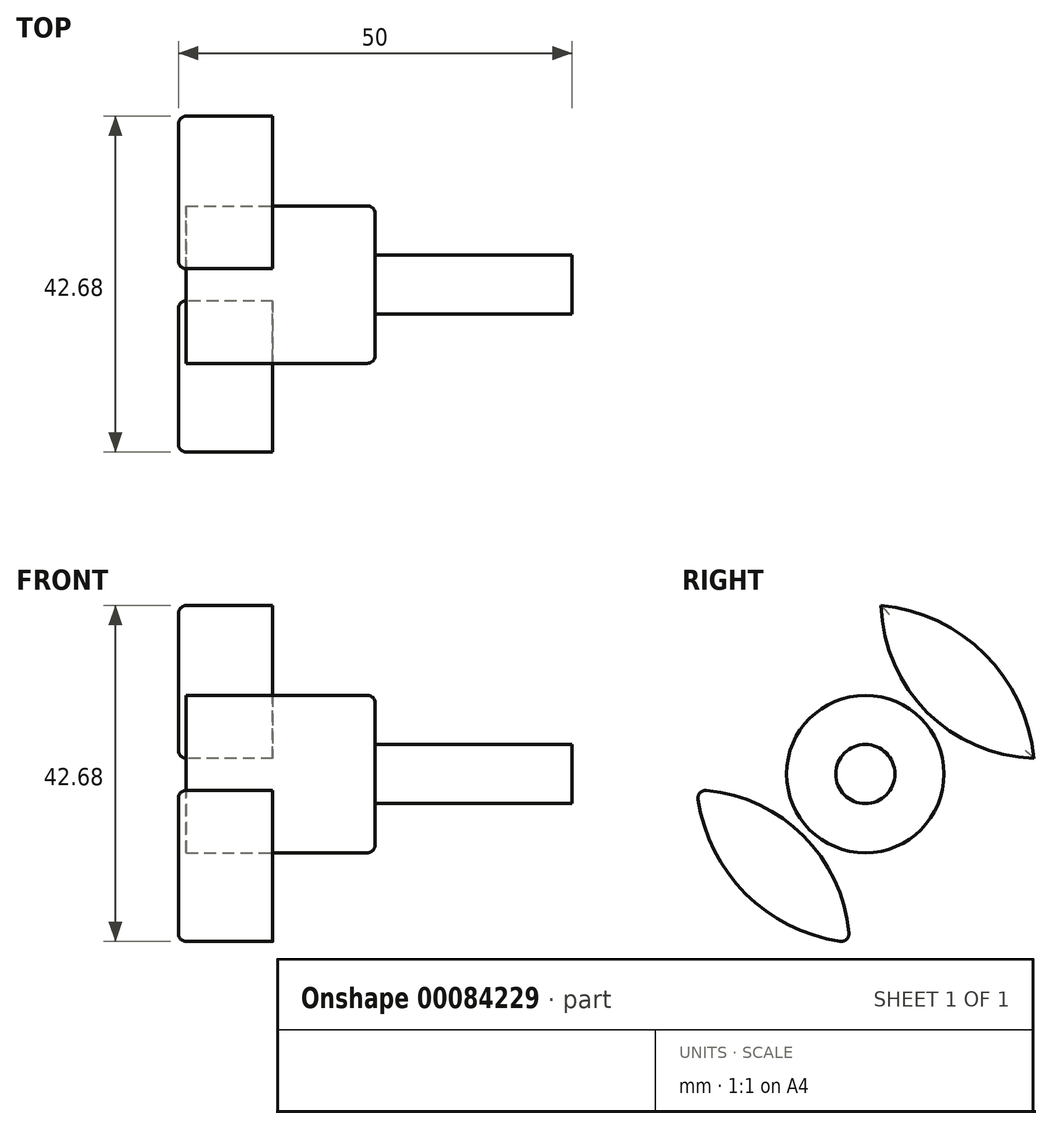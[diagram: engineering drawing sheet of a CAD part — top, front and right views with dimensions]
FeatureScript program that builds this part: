
annotation { "Feature Type Name" : "Feature", "Feature Type Description" : "" }
export const myFeature = defineFeature(function(context is Context, id is Id, definition is map)
    precondition{}
    {
        {
            var Q0;
            Q0=qCreatedBy(makeId("Front.planeOp"),FACE);
            var sketch = newSketch(context, id + "F0", { "sketchPlane" : qUnion([Q0])});
            skLineSegment(sketch, "E0.bottom", {"start": v(0, 0) * mm, "end": v(-25, 0) * mm});
            skLineSegment(sketch, "E0.top", {"start": v(0, 3.75) * mm, "end": v(-25, 3.75) * mm});
            skLineSegment(sketch, "E0.left", {"start": v(0, 0) * mm, "end": v(0, 3.75) * mm});
            skLineSegment(sketch, "E0.right", {"start": v(-25, 0) * mm, "end": v(-25, 3.75) * mm});
            skLineSegment(sketch, "E1.bottom", {"start": v(-25, 0) * mm, "end": v(-38, 0) * mm});
            skLineSegment(sketch, "E1.top", {"start": v(-25, 10) * mm, "end": v(-38, 10) * mm});
            skLineSegment(sketch, "E1.left", {"start": v(-25, 0) * mm, "end": v(-25, 10) * mm});
            skLineSegment(sketch, "E1.right", {"start": v(-38, 0) * mm, "end": v(-38, 10) * mm});
            skLineSegment(sketch, "E2.bottom", {"start": v(-38, 0) * mm, "end": v(-50, 0) * mm});
            skLineSegment(sketch, "E2.top", {"start": v(-38, 21.5) * mm, "end": v(-50, 21.5) * mm});
            skLineSegment(sketch, "E2.left", {"start": v(-38, 0) * mm, "end": v(-38, 21.5) * mm});
            skLineSegment(sketch, "E2.right", {"start": v(-50, 0) * mm, "end": v(-50, 21.5) * mm});
            skLineSegment(sketch, "E3", {"start": v(0, 0) * mm, "end": v(-63.49, 0) * mm, "construction": true});
            skSolve(sketch);
        }
        {
            var Q0;
            {var subQ3=sQuery(id+"F0.wireOp",EDGE,"E2.bottom");Q0=makeQuery(id+"F0.imprint","IMPRINT",FACE,{"disambiguationData":[TD([[makeQuery(id+"F0.imprint","IMPRINT",EDGE,{"derivedFrom":subQ3}),-1.0]])]});}
            var Q1;
            {var subQ3=sQuery(id+"F0.wireOp",EDGE,"E1.bottom");Q1=makeQuery(id+"F0.imprint","IMPRINT",FACE,{"disambiguationData":[TD([[makeQuery(id+"F0.imprint","IMPRINT",EDGE,{"derivedFrom":subQ3}),-1.0]])]});}
            var Q2;
            {var subQ0=sQuery(id+"F0.wireOp",EDGE,"E0.bottom");Q2=makeQuery(id+"F0.imprint","IMPRINT",FACE,{"disambiguationData":[TD([[makeQuery(id+"F0.imprint","IMPRINT",EDGE,{"derivedFrom":subQ0}),-1.0]])]});}
            var Q3;
            Q3=sQuery(id+"F0.wireOp",EDGE,"E3");
            revolve(context, id + "F1", {"entities" : qUnion([Q0, Q1, Q2]), "axis" : qUnion([Q3]), "revolveType" : RevolveType.FULL});
        }
        {
            var Q0;
            Q0=makeQuery(id+"F1.opRevolve","SWEPT_FACE",FACE,{"disambiguationData":[OSD([sQuery(id+"F0.wireOp",EDGE,"E2.right")])]});
            var sketch = newSketch(context, id + "F2", { "sketchPlane" : qUnion([Q0])});
            skCircle(sketch, "E4.0", {"center": v(0, 0) * mm, "radius": 10 * mm});
            skCircle(sketch, "E5.0", {"center": v(0, 0) * mm, "radius": 21.5 * mm});
            skLineSegment(sketch, "E6", {"start": v(0, 21.5) * mm, "end": v(0, -21.5) * mm, "construction": true});
            skLineSegment(sketch, "E7", {"start": v(21.5, 0) * mm, "end": v(-21.5, 0) * mm, "construction": true});
            skLineSegment(sketch, "E8", {"start": v(0, 0) * mm, "end": v(15.2, 15.2) * mm, "construction": true});
            skArc(sketch, "E9", {"start": v(2, 21.4) * mm, "mid": v(7.85, 7.85) * mm, "end": v(21.4, 2) * mm});
            skArc(sketch, "E10.MirrorCS", {"start": v(2, -21.4) * mm, "mid": v(7.85, -7.85) * mm, "end": v(21.4, -2) * mm});
            skArc(sketch, "E11.MirrorCS", {"start": v(-2, 21.4) * mm, "mid": v(-7.85, 7.85) * mm, "end": v(-21.4, 2) * mm});
            skArc(sketch, "E12.MirrorCS", {"start": v(-2, -21.4) * mm, "mid": v(-7.85, -7.85) * mm, "end": v(-21.4, -2) * mm});
            skSolve(sketch);
        }
        {
            var Q0;
            {var subQ0=sQuery(id+"F2.wireOp",EDGE,"E11.MirrorCS");Q0=makeQuery(id+"F2.imprint","IMPRINT",FACE,{"disambiguationData":[TD([[makeQuery(id+"F2.imprint","IMPRINT",EDGE,{"derivedFrom":subQ0}),-1.0]])]});}
            var Q1;
            {var subQ0=sQuery(id+"F2.wireOp",EDGE,"E9");Q1=makeQuery(id+"F2.imprint","IMPRINT",FACE,{"disambiguationData":[TD([[makeQuery(id+"F2.imprint","IMPRINT",EDGE,{"derivedFrom":subQ0}),1.0]])]});}
            var Q2;
            {var subQ0=sQuery(id+"F2.wireOp",EDGE,"E12.MirrorCS");Q2=makeQuery(id+"F2.imprint","IMPRINT",FACE,{"disambiguationData":[TD([[makeQuery(id+"F2.imprint","IMPRINT",EDGE,{"derivedFrom":subQ0}),1.0]])]});}
            var Q3;
            {var subQ0=sQuery(id+"F2.wireOp",EDGE,"E10.MirrorCS");Q3=makeQuery(id+"F2.imprint","IMPRINT",FACE,{"disambiguationData":[TD([[makeQuery(id+"F2.imprint","IMPRINT",EDGE,{"derivedFrom":subQ0}),-1.0]])]});}
            extrude(context, id + "F3", {"entities" : qUnion([Q0, Q1, Q2, Q3]), "operationType" : NewBodyOperationType.REMOVE, "endBound" : BoundingType.THROUGH_ALL, "oppositeDirection" : true, "depth" : 25 * mm});
        }
        {
            var Q0;
            Q0=makeQuery(id+"F1.opRevolve","SWEPT_FACE",FACE,{"disambiguationData":[OSD([sQuery(id+"F0.wireOp",EDGE,"E2.right")])]});
            var Q1;
            {var subQ0=sQuery(id+"F2.wireOp",EDGE,"E10.MirrorCS");var subQ1=sQuery(id+"F2.wireOp",EDGE,"E5.0");Q1=makeQuery(id+"F3.boolean.opBoolean","COPY",EDGE,{"derivedFrom":makeQuery(id+"F3.opExtrude","SWEPT_EDGE",EDGE,{"disambiguationData":[OSD([subQ1,subQ0]),TDD([makeQuery(id+"F2.imprint","INTERSECT",VERTEX,{"disambiguationData":[OD(0.0)],"derivedFrom":[subQ1,subQ0]})])]})});}
            var Q2;
            {var subQ0=sQuery(id+"F2.wireOp",EDGE,"E12.MirrorCS");var subQ1=sQuery(id+"F2.wireOp",EDGE,"E5.0");Q2=makeQuery(id+"F3.boolean.opBoolean","COPY",EDGE,{"derivedFrom":makeQuery(id+"F3.opExtrude","SWEPT_EDGE",EDGE,{"disambiguationData":[OSD([subQ1,subQ0]),TDD([makeQuery(id+"F2.imprint","INTERSECT",VERTEX,{"disambiguationData":[OD(0.0)],"derivedFrom":[subQ1,subQ0]})])]})});}
            var Q3;
            {var subQ0=sQuery(id+"F2.wireOp",EDGE,"E10.MirrorCS");var subQ1=sQuery(id+"F2.wireOp",EDGE,"E5.0");Q3=makeQuery(id+"F3.boolean.opBoolean","COPY",EDGE,{"derivedFrom":makeQuery(id+"F3.opExtrude","SWEPT_EDGE",EDGE,{"disambiguationData":[OSD([subQ1,subQ0]),TDD([makeQuery(id+"F2.imprint","INTERSECT",VERTEX,{"disambiguationData":[OD(1.0)],"derivedFrom":[subQ1,subQ0]})])]})});}
            var Q4;
            {var subQ0=sQuery(id+"F2.wireOp",EDGE,"E9");var subQ1=sQuery(id+"F2.wireOp",EDGE,"E5.0");Q4=makeQuery(id+"F3.boolean.opBoolean","COPY",EDGE,{"derivedFrom":makeQuery(id+"F3.opExtrude","SWEPT_EDGE",EDGE,{"disambiguationData":[OSD([subQ1,subQ0]),TDD([makeQuery(id+"F2.imprint","INTERSECT",VERTEX,{"disambiguationData":[OD(1.0)],"derivedFrom":[subQ1,subQ0]})])]})});}
            var Q5;
            {var subQ0=sQuery(id+"F2.wireOp",EDGE,"E9");var subQ1=sQuery(id+"F2.wireOp",EDGE,"E5.0");Q5=makeQuery(id+"F3.boolean.opBoolean","COPY",EDGE,{"derivedFrom":makeQuery(id+"F3.opExtrude","SWEPT_EDGE",EDGE,{"disambiguationData":[OSD([subQ1,subQ0]),TDD([makeQuery(id+"F2.imprint","INTERSECT",VERTEX,{"disambiguationData":[OD(0.0)],"derivedFrom":[subQ1,subQ0]})])]})});}
            var Q6;
            {var subQ0=sQuery(id+"F2.wireOp",EDGE,"E11.MirrorCS");var subQ1=sQuery(id+"F2.wireOp",EDGE,"E5.0");Q6=makeQuery(id+"F3.boolean.opBoolean","COPY",EDGE,{"derivedFrom":makeQuery(id+"F3.opExtrude","SWEPT_EDGE",EDGE,{"disambiguationData":[OSD([subQ1,subQ0]),TDD([makeQuery(id+"F2.imprint","INTERSECT",VERTEX,{"disambiguationData":[OD(0.0)],"derivedFrom":[subQ1,subQ0]})])]})});}
            var Q7;
            {var subQ0=sQuery(id+"F2.wireOp",EDGE,"E11.MirrorCS");var subQ1=sQuery(id+"F2.wireOp",EDGE,"E5.0");Q7=makeQuery(id+"F3.boolean.opBoolean","COPY",EDGE,{"derivedFrom":makeQuery(id+"F3.opExtrude","SWEPT_EDGE",EDGE,{"disambiguationData":[OSD([subQ1,subQ0]),TDD([makeQuery(id+"F2.imprint","INTERSECT",VERTEX,{"disambiguationData":[OD(1.0)],"derivedFrom":[subQ1,subQ0]})])]})});}
            var Q8;
            {var subQ0=sQuery(id+"F2.wireOp",EDGE,"E12.MirrorCS");var subQ1=sQuery(id+"F2.wireOp",EDGE,"E5.0");Q8=makeQuery(id+"F3.boolean.opBoolean","COPY",EDGE,{"derivedFrom":makeQuery(id+"F3.opExtrude","SWEPT_EDGE",EDGE,{"disambiguationData":[OSD([subQ1,subQ0]),TDD([makeQuery(id+"F2.imprint","INTERSECT",VERTEX,{"disambiguationData":[OD(1.0)],"derivedFrom":[subQ1,subQ0]})])]})});}
            var Q9;
            Q9=makeQuery(id+"F1.opRevolve","SWEPT_EDGE",EDGE,{"disambiguationData":[OSD([sQuery(id+"F0.wireOp",EDGE,"E1.top"),sQuery(id+"F0.wireOp",EDGE,"E1.left")])]});
            fillet(context, id + "F4", {"entities" : qUnion([Q0, Q1, Q2, Q3, Q4, Q5, Q6, Q7, Q8, Q9]), "radius" : 1 * mm, "tangentPropagation" : true, "allowEdgeOverflow" : false});
        }
        {
            var Q0;
            Q0=makeQuery(id+"F2.imprint","IMPRINT",FACE,{"disambiguationData":[TD([[makeQuery(id+"F2.imprint","IMPRINT",EDGE,{"derivedFrom":sQuery(id+"F2.wireOp",EDGE,"E4.0")}),1.0]])]});
            extrude(context, id + "F5", {"entities" : qUnion([Q0]), "operationType" : NewBodyOperationType.REMOVE, "oppositeDirection" : true, "depth" : 1 * mm});
        }
    });
